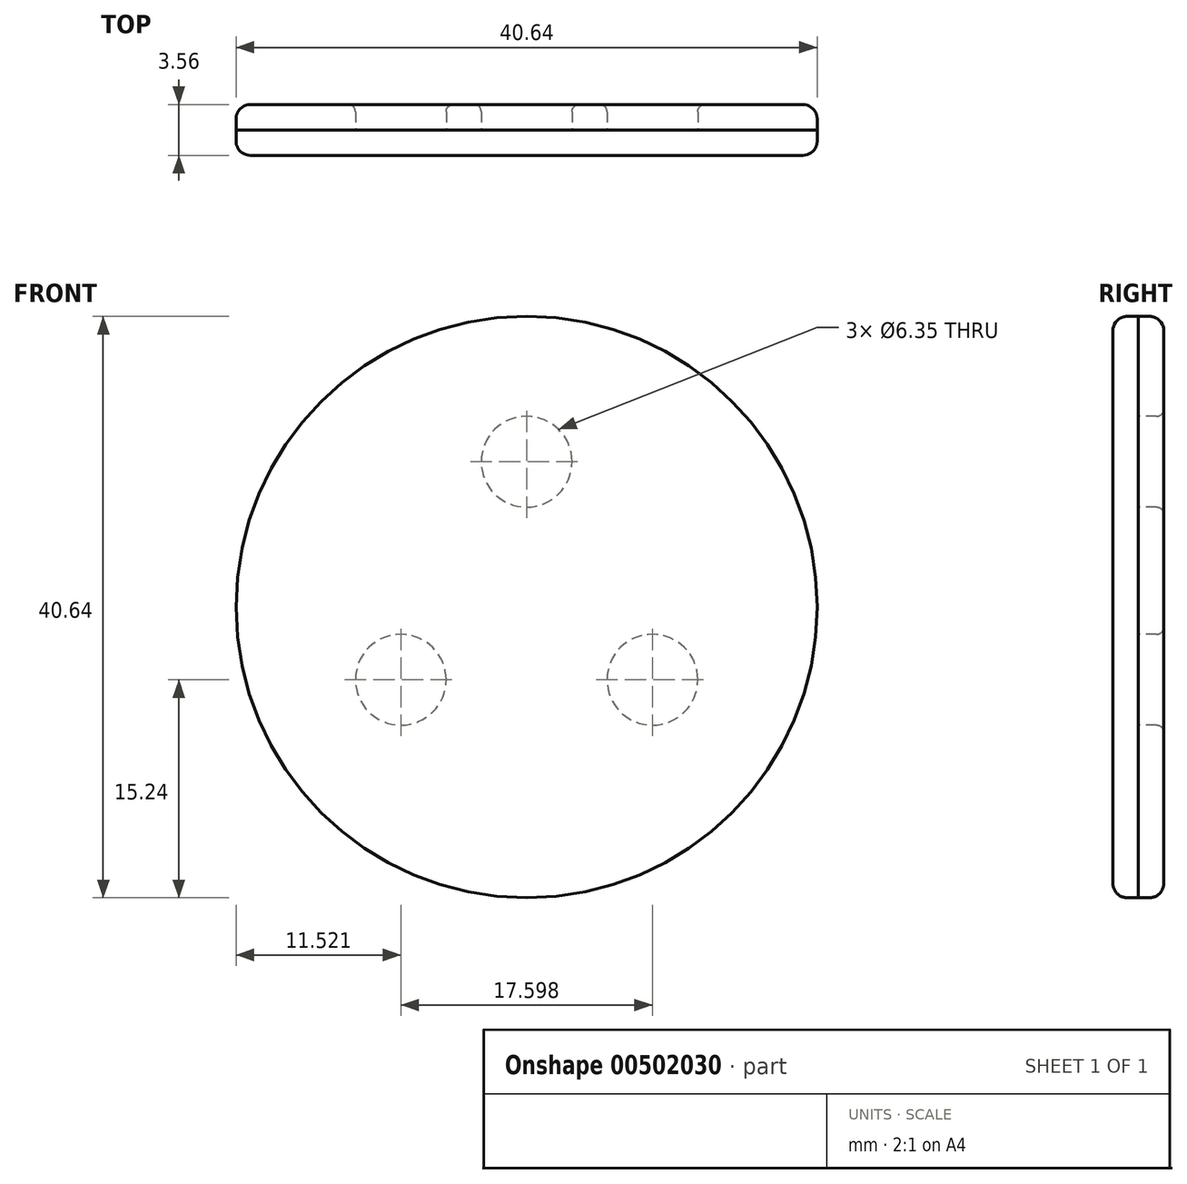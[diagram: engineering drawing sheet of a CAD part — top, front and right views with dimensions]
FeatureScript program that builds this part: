
annotation { "Feature Type Name" : "Feature", "Feature Type Description" : "" }
export const myFeature = defineFeature(function(context is Context, id is Id, definition is map)
    precondition{}
    {
        {
            var Q0;
            Q0=qCreatedBy(makeId("Front.planeOp"),FACE);
            var sketch = newSketch(context, id + "F0", { "sketchPlane" : qUnion([Q0])});
            skCircle(sketch, "E0", {"center": v(0, 0) * mm, "radius": 20.32 * mm});
            skCircle(sketch, "E1", {"center": v(0, 0) * mm, "radius": 17.78 * mm});
            skPoint(sketch, "E2", {"position": v(0, 10.16) * mm});
            skPoint(sketch, "E3.1.0", {"position": v(-8.8, -5.08) * mm});
            skPoint(sketch, "E3.2.0", {"position": v(8.8, -5.08) * mm});
            skCircle(sketch, "E4", {"center": v(-8.8, -5.08) * mm, "radius": 3.18 * mm});
            skCircle(sketch, "E5", {"center": v(0, 10.16) * mm, "radius": 3.18 * mm});
            skCircle(sketch, "E6", {"center": v(8.8, -5.08) * mm, "radius": 3.18 * mm});
            skSolve(sketch);
        }
        {
            var Q0;
            Q0=makeQuery(id+"F0.imprint","IMPRINT",FACE,{"disambiguationData":[TD([[makeQuery(id+"F0.imprint","IMPRINT",EDGE,{"derivedFrom":sQuery(id+"F0.wireOp",EDGE,"E1")}),1.0]])]});
            var Q1;
            Q1=makeQuery(id+"F0.imprint","IMPRINT",FACE,{"disambiguationData":[TD([[makeQuery(id+"F0.imprint","IMPRINT",EDGE,{"derivedFrom":sQuery(id+"F0.wireOp",EDGE,"E0")}),1.0]])]});
            var Q2;
            Q2=makeQuery(id+"F0.imprint","IMPRINT",FACE,{"disambiguationData":[TD([[makeQuery(id+"F0.imprint","IMPRINT",EDGE,{"derivedFrom":sQuery(id+"F0.wireOp",EDGE,"E4")}),1.0]])]});
            var Q3;
            Q3=makeQuery(id+"F0.imprint","IMPRINT",FACE,{"disambiguationData":[TD([[makeQuery(id+"F0.imprint","IMPRINT",EDGE,{"derivedFrom":sQuery(id+"F0.wireOp",EDGE,"E6")}),1.0]])]});
            var Q4;
            Q4=makeQuery(id+"F0.imprint","IMPRINT",FACE,{"disambiguationData":[TD([[makeQuery(id+"F0.imprint","IMPRINT",EDGE,{"derivedFrom":sQuery(id+"F0.wireOp",EDGE,"E5")}),1.0]])]});
            extrude(context, id + "F1", {"entities" : qUnion([Q0, Q1, Q2, Q3, Q4]), "depth" : 1.78 * mm, "offsetDistance" : 25.4 * mm});
        }
        {
            var Q0;
            Q0=makeQuery(id+"F0.imprint","IMPRINT",FACE,{"disambiguationData":[TD([[makeQuery(id+"F0.imprint","IMPRINT",EDGE,{"derivedFrom":sQuery(id+"F0.wireOp",EDGE,"E1")}),1.0]])]});
            var Q1;
            Q1=makeQuery(id+"F0.imprint","IMPRINT",FACE,{"disambiguationData":[TD([[makeQuery(id+"F0.imprint","IMPRINT",EDGE,{"derivedFrom":sQuery(id+"F0.wireOp",EDGE,"E0")}),1.0]])]});
            extrude(context, id + "F2", {"entities" : qUnion([Q0, Q1]), "oppositeDirection" : true, "depth" : 1.78 * mm, "offsetDistance" : 25.4 * mm});
        }
        {
            var Q0;
            Q0=makeQuery(id+"F1.opExtrude","CAP_EDGE",EDGE,{"disambiguationData":[OSD([sQuery(id+"F0.wireOp",EDGE,"E0")])],"isStart":false});
            var Q1;
            Q1=makeQuery(id+"F2.opExtrude","CAP_EDGE",EDGE,{"disambiguationData":[OSD([sQuery(id+"F0.wireOp",EDGE,"E0")])],"isStart":false});
            fillet(context, id + "F3", {"entities" : qUnion([Q0, Q1]), "radius" : 1 * mm, "tangentPropagation" : true, "allowEdgeOverflow" : false});
        }
        {
            var Q0;
            Q0=makeQuery(id+"F2.opExtrude","CAP_EDGE",EDGE,{"disambiguationData":[OSD([sQuery(id+"F0.wireOp",EDGE,"E6")])],"isStart":false});
            var Q1;
            Q1=makeQuery(id+"F2.opExtrude","CAP_EDGE",EDGE,{"disambiguationData":[OSD([sQuery(id+"F0.wireOp",EDGE,"E4")])],"isStart":false});
            var Q2;
            Q2=makeQuery(id+"F2.opExtrude","CAP_EDGE",EDGE,{"disambiguationData":[OSD([sQuery(id+"F0.wireOp",EDGE,"E5")])],"isStart":false});
            fillet(context, id + "F4", {"entities" : qUnion([Q0, Q1, Q2]), "radius" : 0.5 * mm, "tangentPropagation" : true, "allowEdgeOverflow" : false});
        }
    });
